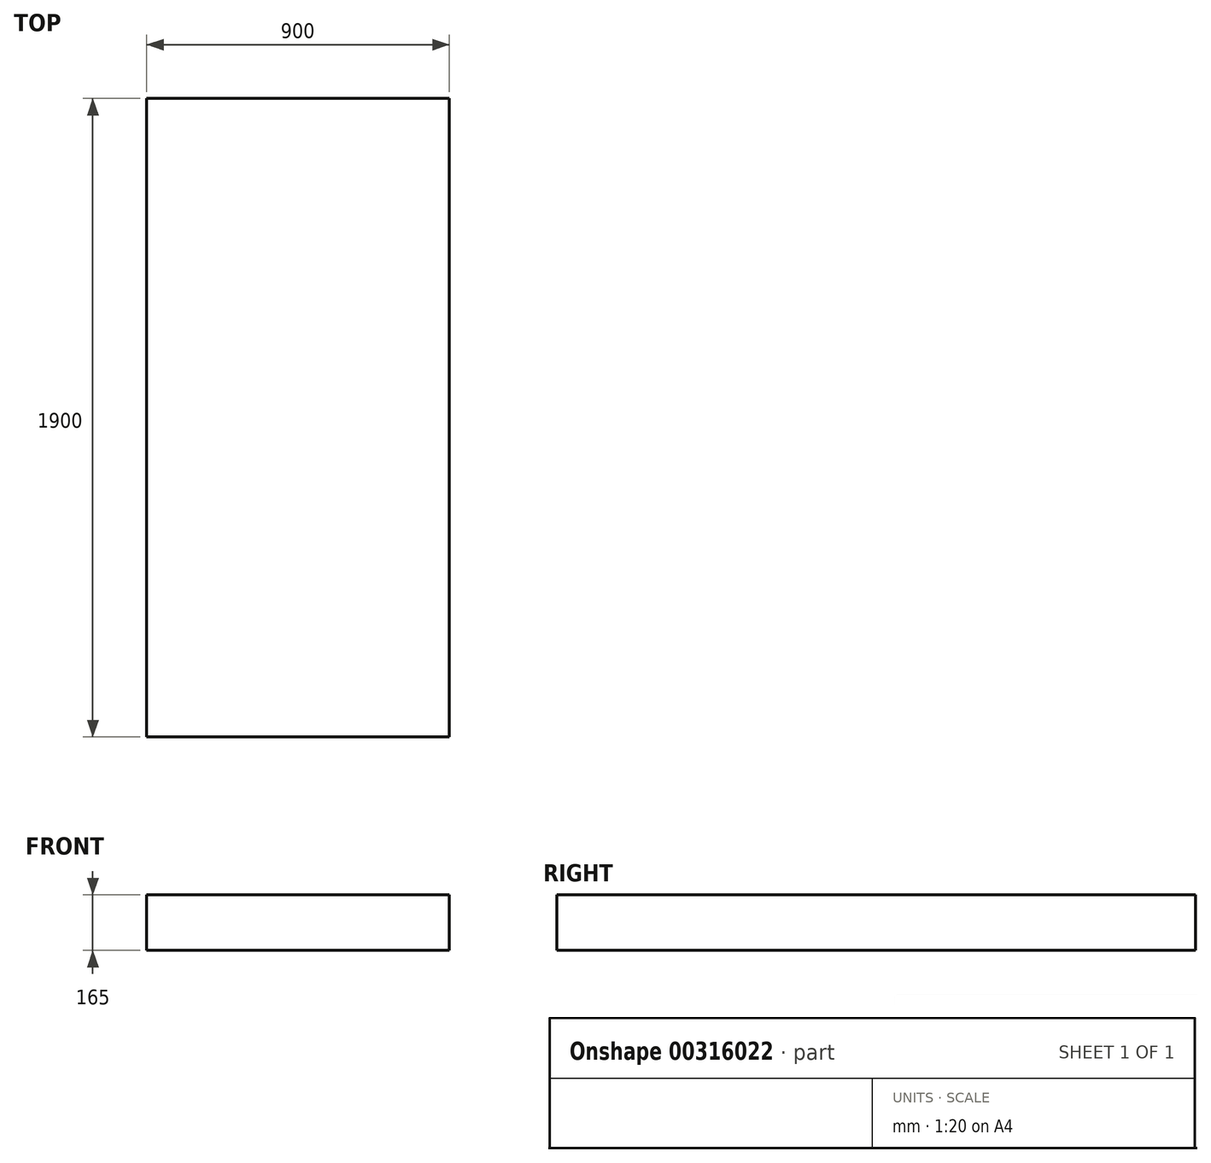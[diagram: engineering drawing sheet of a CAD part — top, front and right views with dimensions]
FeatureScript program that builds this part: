
annotation { "Feature Type Name" : "Feature", "Feature Type Description" : "" }
export const myFeature = defineFeature(function(context is Context, id is Id, definition is map)
    precondition{}
    {
        {
            var Q0;
            Q0=qCreatedBy(makeId("Front.planeOp"),FACE);
            var sketch = newSketch(context, id + "F0", { "sketchPlane" : qUnion([Q0])});
            skLineSegment(sketch, "E0.bottom", {"start": v(0, 0) * mm, "end": v(900, 0) * mm});
            skLineSegment(sketch, "E0.top", {"start": v(0, 165) * mm, "end": v(900, 165) * mm});
            skLineSegment(sketch, "E0.left", {"start": v(0, 0) * mm, "end": v(0, 165) * mm});
            skLineSegment(sketch, "E0.right", {"start": v(900, 0) * mm, "end": v(900, 165) * mm});
            skSolve(sketch);
        }
        {
            var Q0;
            Q0=qSketchRegion(id+"F0",true);
            extrude(context, id + "F1", {"entities" : qUnion([Q0]), "depth" : 1900 * mm});
        }
    });
